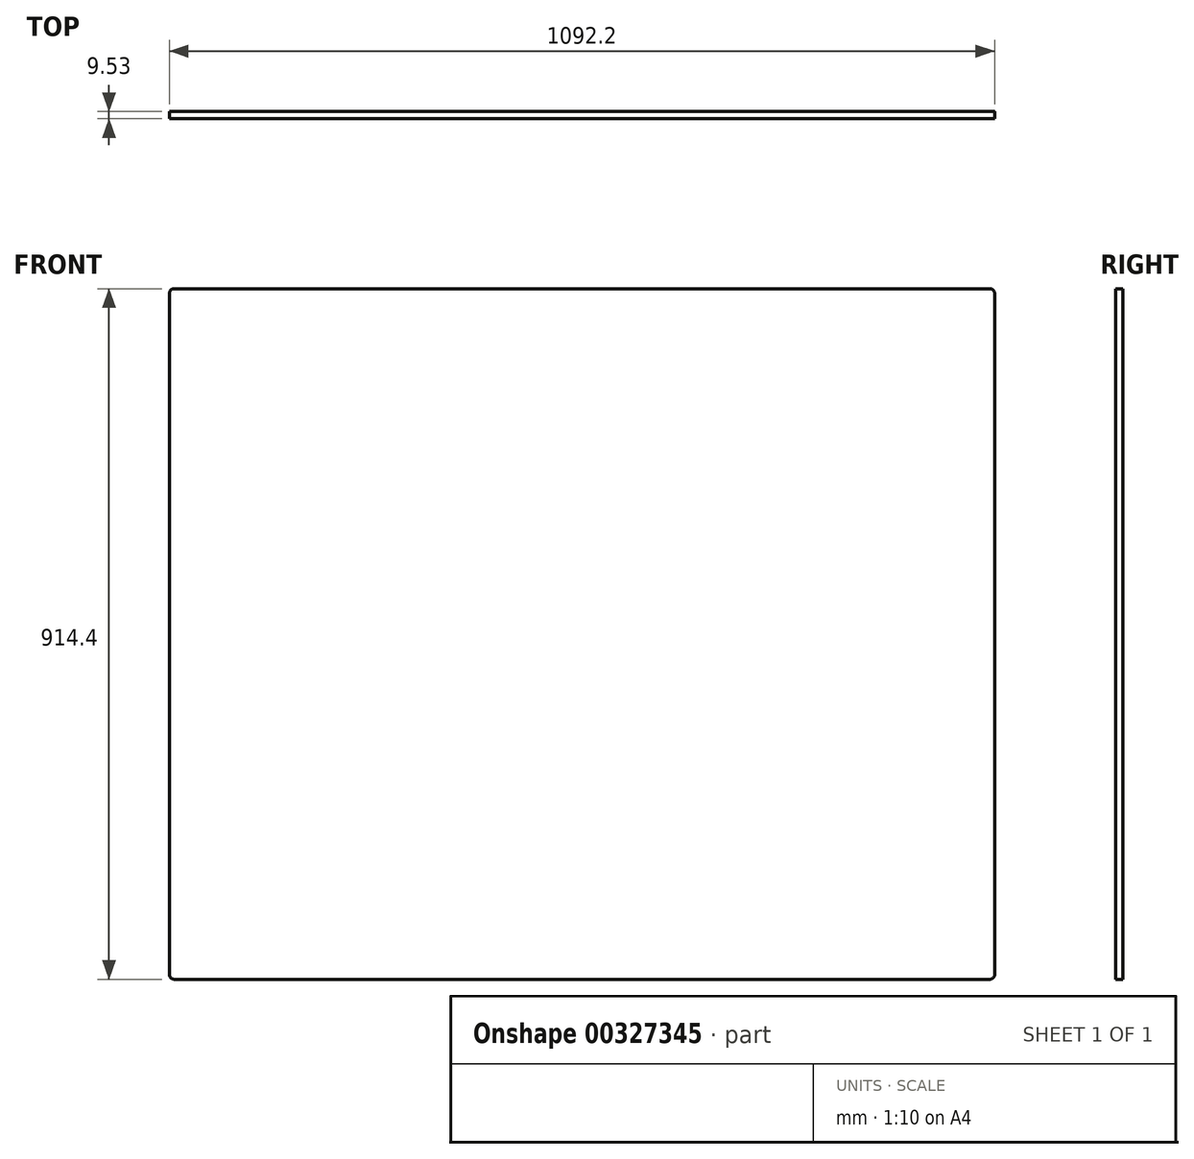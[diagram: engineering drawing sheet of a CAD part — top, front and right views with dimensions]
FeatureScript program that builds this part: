
annotation { "Feature Type Name" : "Feature", "Feature Type Description" : "" }
export const myFeature = defineFeature(function(context is Context, id is Id, definition is map)
    precondition{}
    {
        {
            var Q0;
            Q0=qCreatedBy(makeId("Front.planeOp"),FACE);
            var sketch = newSketch(context, id + "F0", { "sketchPlane" : qUnion([Q0])});
            skLineSegment(sketch, "E0.bottom", {"start": v(0, 0) * mm, "end": v(0, 0) * mm});
            skLineSegment(sketch, "E1.bottom", {"start": v(-602.73, 313.18) * mm, "end": v(476.77, 313.18) * mm});
            skLineSegment(sketch, "E1.top", {"start": v(-602.73, -601.22) * mm, "end": v(476.77, -601.22) * mm});
            skLineSegment(sketch, "E1.left", {"start": v(-609.08, 306.83) * mm, "end": v(-609.08, -594.87) * mm});
            skLineSegment(sketch, "E1.right", {"start": v(483.12, 306.83) * mm, "end": v(483.12, -594.87) * mm});
            skPoint(sketch, "E2.visualSharp", {"position": v(-609.08, 313.18) * mm});
            skArc(sketch, "E2.filletArc", {"start": v(-602.73, 313.18) * mm, "mid": v(-607.22, 311.32) * mm, "end": v(-609.08, 306.83) * mm});
            skPoint(sketch, "E3.visualSharp", {"position": v(483.12, 313.18) * mm});
            skArc(sketch, "E3.filletArc", {"start": v(483.12, 306.83) * mm, "mid": v(481.26, 311.32) * mm, "end": v(476.77, 313.18) * mm});
            skPoint(sketch, "E4.visualSharp", {"position": v(483.12, -601.22) * mm});
            skArc(sketch, "E4.filletArc", {"start": v(476.77, -601.22) * mm, "mid": v(481.26, -599.36) * mm, "end": v(483.12, -594.87) * mm});
            skPoint(sketch, "E5.visualSharp", {"position": v(-609.08, -601.22) * mm});
            skArc(sketch, "E5.filletArc", {"start": v(-609.08, -594.87) * mm, "mid": v(-607.22, -599.36) * mm, "end": v(-602.73, -601.22) * mm});
            skSolve(sketch);
        }
        {
            var Q0;
            Q0=makeQuery(id+"F0.imprint","IMPRINT",FACE,{"disambiguationData":[TD([[makeQuery(id+"F0.imprint","IMPRINT",EDGE,{"derivedFrom":sQuery(id+"F0.wireOp",EDGE,"E1.bottom")}),-1.0]])]});
            extrude(context, id + "F1", {"entities" : qUnion([Q0]), "depth" : 9.52 * mm});
        }
    });
